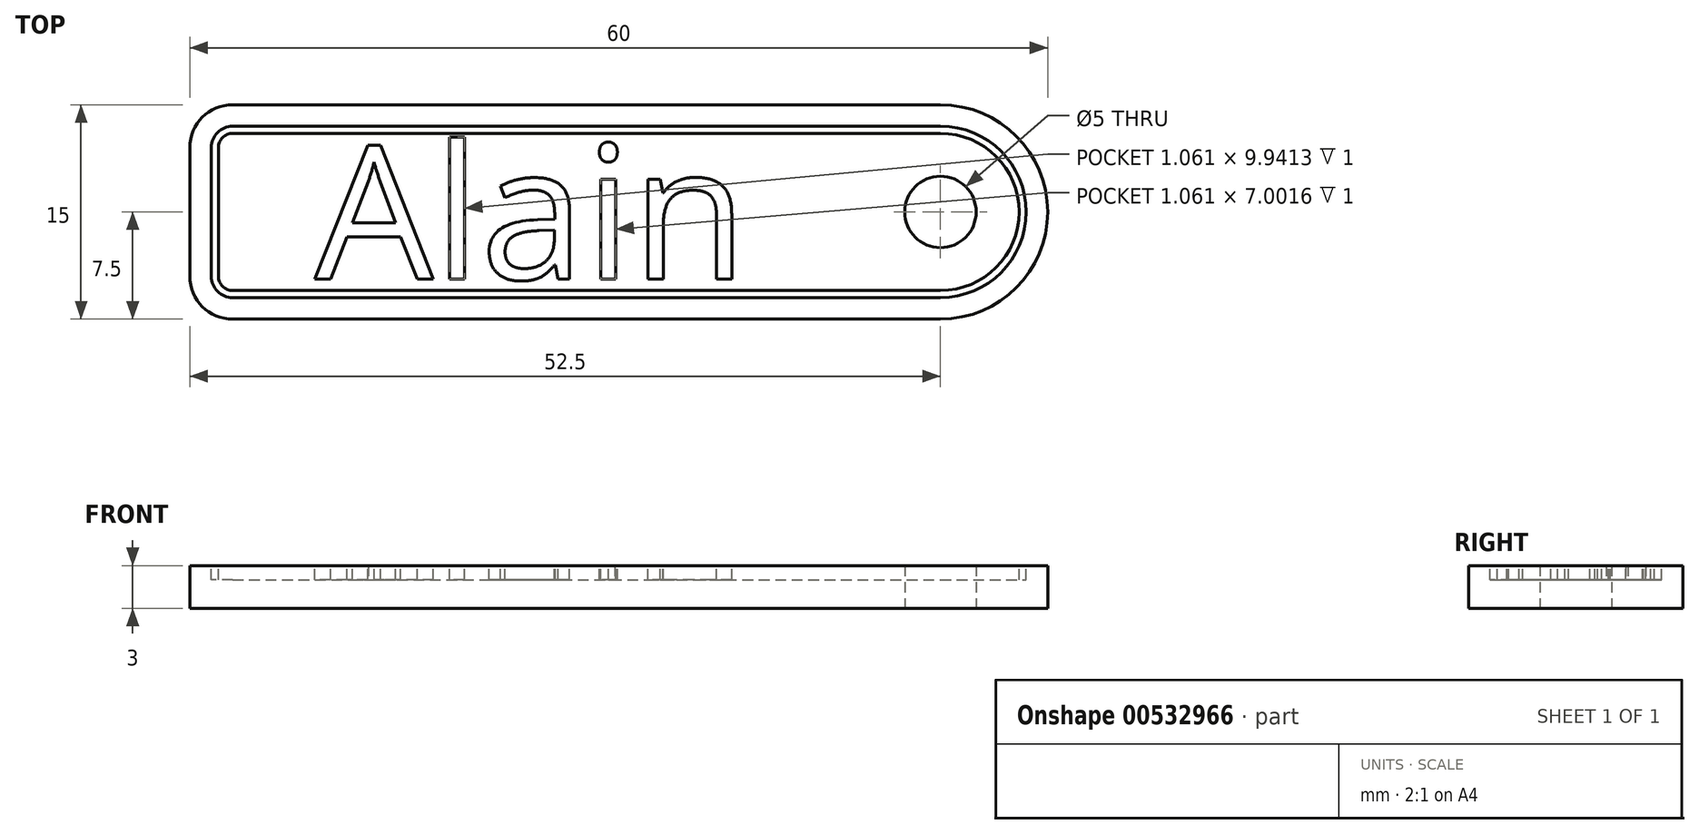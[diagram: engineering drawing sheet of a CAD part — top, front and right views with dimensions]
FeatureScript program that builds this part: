
annotation { "Feature Type Name" : "Feature", "Feature Type Description" : "" }
export const myFeature = defineFeature(function(context is Context, id is Id, definition is map)
    precondition{}
    {
        {
            var Q0;
            Q0=qCreatedBy(makeId("Top.planeOp"),FACE);
            var sketch = newSketch(context, id + "F0", { "sketchPlane" : qUnion([Q0])});
            skLineSegment(sketch, "E0.bottom", {"start": v(-27, 7.5) * mm, "end": v(22.5, 7.5) * mm});
            skLineSegment(sketch, "E0.top", {"start": v(-27, -7.5) * mm, "end": v(22.5, -7.5) * mm});
            skLineSegment(sketch, "E0.left", {"start": v(-30, 4.5) * mm, "end": v(-30, -4.5) * mm});
            skArc(sketch, "E1", {"start": v(22.5, 7.5) * mm, "mid": v(30, 0) * mm, "end": v(22.5, -7.5) * mm});
            skPoint(sketch, "E2.visualSharp", {"position": v(-30, 7.5) * mm});
            skArc(sketch, "E2.filletArc", {"start": v(-27, 7.5) * mm, "mid": v(-29.12, 6.62) * mm, "end": v(-30, 4.5) * mm});
            skPoint(sketch, "E3.visualSharp", {"position": v(-30, -7.5) * mm});
            skArc(sketch, "E3.filletArc", {"start": v(-30, -4.5) * mm, "mid": v(-29.12, -6.62) * mm, "end": v(-27, -7.5) * mm});
            skCircle(sketch, "E4", {"center": v(22.5, 0) * mm, "radius": 2.5 * mm});
            skLineSegment(sketch, "E5", {"start": v(30, 15.32) * mm, "end": v(30, -25.88) * mm, "construction": true});
            skPoint(sketch, "E5.startSnap0", {"position": v(30, 0) * mm});
            skSolve(sketch);
        }
        {
            var Q0;
            Q0 = qSketchRegion(id + "F0", true);
            extrude(context, id + "F1", {"entities" : qUnion([Q0]), "depth" : 3 * mm, "offsetDistance" : 25 * mm});
        }
        {
            var Q0;
            Q0=makeQuery(id+"F1.opExtrude","CAP_FACE",FACE,{"disambiguationData":[OSD([sQuery(id+"F0.wireOp",EDGE,"E0.bottom"),sQuery(id+"F0.wireOp",EDGE,"E0.top"),sQuery(id+"F0.wireOp",EDGE,"E0.left"),sQuery(id+"F0.wireOp",EDGE,"E1"),sQuery(id+"F0.wireOp",EDGE,"E2.filletArc"),sQuery(id+"F0.wireOp",EDGE,"E3.filletArc"),sQuery(id+"F0.wireOp",EDGE,"E4")])],"isStart":false});
            var sketch = newSketch(context, id + "F2", { "sketchPlane" : qUnion([Q0])});
            skText(sketch, "E6", { "text": "Alain\n", "fontName": "OpenSans-Regular.ttf"});
            const initialGuessF2  = {"E6": [-0.02125, -0.00471, 1, 0, 0.00942]};
            skSetInitialGuess(sketch, initialGuessF2);
            skSolve(sketch);
        }
        {
            var Q0;
            Q0 = qSketchRegion(id + "F2", true);
            extrude(context, id + "F3", {"entities" : qUnion([Q0]), "operationType" : NewBodyOperationType.REMOVE, "oppositeDirection" : true, "depth" : 1 * mm, "offsetDistance" : 25 * mm});
        }
        {
            var Q0;
            {var subQ0=sQuery(id+"F0.wireOp",EDGE,"E0.left");var subQ1=sQuery(id+"F0.wireOp",EDGE,"E4");var subQ2=sQuery(id+"F0.wireOp",EDGE,"E3.filletArc");var subQ3=sQuery(id+"F0.wireOp",EDGE,"E2.filletArc");var subQ4=sQuery(id+"F0.wireOp",EDGE,"E0.bottom");var subQ5=sQuery(id+"F0.wireOp",EDGE,"E1");var subQ6=sQuery(id+"F0.wireOp",EDGE,"E0.top");Q0=makeQuery(id+"F3.boolean.opBoolean","SPLIT",FACE,{"disambiguationData":[TD([makeQuery(id+"F1.opExtrude","SWEPT_FACE",FACE,{"disambiguationData":[OSD([subQ4])]})])],"derivedFrom":makeQuery(id+"F1.opExtrude","CAP_FACE",FACE,{"disambiguationData":[OSD([subQ4,subQ6,subQ0,subQ5,subQ3,subQ2,subQ1])],"isStart":false})});}
            var sketch = newSketch(context, id + "F4", { "sketchPlane" : qUnion([Q0])});
            skSolve(sketch);
        }
        {
            var Q0;
            Q0=makeQuery(id+"F4.imprint","IMPRINT",FACE,{"disambiguationData":[TD([[makeQuery(id+"F4.imprint","IMPRINT",EDGE,{"derivedFrom":makeQuery(id+"F1.opExtrude","CAP_EDGE",EDGE,{"disambiguationData":[OSD([sQuery(id+"F0.wireOp",EDGE,"E0.bottom")])],"isStart":false})}),-1.0]])]});
            var sketch = newSketch(context, id + "F5", { "sketchPlane" : qUnion([Q0])});
            skArc(sketch, "E7.0", {"start": v(-27, 6) * mm, "mid": v(-28.06, 5.56) * mm, "end": v(-28.5, 4.5) * mm});
            skArc(sketch, "E7.1", {"start": v(22.5, 6) * mm, "mid": v(28.5, 0) * mm, "end": v(22.5, -6) * mm});
            skLineSegment(sketch, "E7.2", {"start": v(-27, -6) * mm, "end": v(22.5, -6) * mm});
            skLineSegment(sketch, "E7.3", {"start": v(-27, 6) * mm, "end": v(22.5, 6) * mm});
            skArc(sketch, "E7.4", {"start": v(-28.5, -4.5) * mm, "mid": v(-28.06, -5.56) * mm, "end": v(-27, -6) * mm});
            skLineSegment(sketch, "E7.5", {"start": v(-28.5, 4.5) * mm, "end": v(-28.5, -4.5) * mm});
            skLineSegment(sketch, "E8.0", {"start": v(-27, 5.5) * mm, "end": v(22.5, 5.5) * mm});
            skLineSegment(sketch, "E8.1", {"start": v(-28, 4.5) * mm, "end": v(-28, -4.5) * mm});
            skLineSegment(sketch, "E8.2", {"start": v(-27, -5.5) * mm, "end": v(22.5, -5.5) * mm});
            skArc(sketch, "E8.3", {"start": v(22.5, 5.5) * mm, "mid": v(28, 0) * mm, "end": v(22.5, -5.5) * mm});
            skPoint(sketch, "E9.visualSharp", {"position": v(-28, 5.5) * mm});
            skArc(sketch, "E9.filletArc", {"start": v(-27, 5.5) * mm, "mid": v(-27.7, 5.2) * mm, "end": v(-28, 4.5) * mm});
            skPoint(sketch, "E10.visualSharp", {"position": v(-28, -5.5) * mm});
            skArc(sketch, "E10.filletArc", {"start": v(-28, -4.5) * mm, "mid": v(-27.7, -5.2) * mm, "end": v(-27, -5.5) * mm});
            skSolve(sketch);
        }
        {
            var Q0;
            Q0 = qSketchRegion(id + "F5", true);
            extrude(context, id + "F6", {"entities" : qUnion([Q0]), "operationType" : NewBodyOperationType.REMOVE, "oppositeDirection" : true, "depth" : 1 * mm, "offsetDistance" : 25 * mm});
        }
    });
